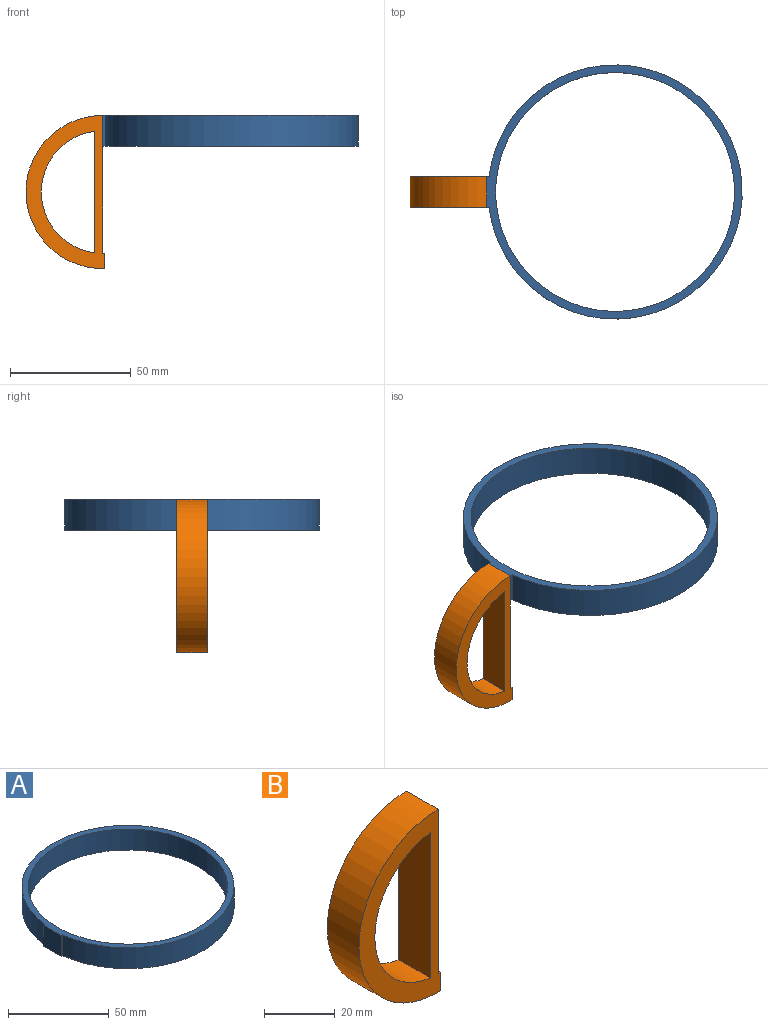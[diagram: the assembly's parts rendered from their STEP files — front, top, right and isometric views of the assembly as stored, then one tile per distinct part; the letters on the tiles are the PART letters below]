
ASSEMBLY  parts=2 mates=1
PART A: 7 faces, bbox 106x105.4x12.7 mm
  f0: plane 12.7x1.02mm, normal (0,-1,0), area 12.9mm2, adj f1,f3,f5,f6
  f1: cylinder r=52.7mm len=105.41mm, axis (0,0,-1), area 4044mm2, adj f0,f2,f5,f6
  f2: plane 12.7x1.02mm, normal (0,1,0), area 12.9mm2, adj f1,f3,f5,f6
  f3: plane 12.7x12.7mm, normal (-1,0,0), area 161.3mm2, adj f0,f2,f5,f6
  f4: cylinder r=49.53mm len=99.06mm, axis (0,0,-1), area 3952.3mm2, adj f5,f6
  f5: plane 106.05x105.41mm, normal (0,0,1), area 1029.4mm2, adj f0,f1,f2,f3,f4
  f6: plane 106.05x105.41mm, normal (0,0,-1), area 1029.4mm2, adj f0,f1,f2,f3,f4
PART B: 9 faces, bbox 32.8x12.7x63.5 mm
  f0: plane 57.15x12.7mm, normal (1,0,0), area 725.8mm2, adj f1,f6,f7,f8
  f1: cylinder r=31.75mm len=63.5mm, axis (0,1,0), area 1279.7mm2, adj f0,f2,f7,f8
  f2: plane 12.7x6.34mm, normal (1,0,0), area 80.5mm2, adj f1,f3,f7,f8
  f3: plane 12.7x0.73mm, normal (0,0,1), area 9.2mm2, adj f2,f6,f7,f8
  f4: cylinder r=25.4mm len=50.4mm, axis (0,1,0), area 932.6mm2, adj f5,f7,f8
  f5: plane 50.4x12.7mm, normal (-1,0,0), area 640.1mm2, adj f4,f7,f8
  f6: cylinder r=25.4mm len=12.7mm, axis (0,1,0), area 3.7mm2, adj f0,f3,f7,f8
  f7: plane 63.5x32.77mm, normal (0,-1,0), area 737.4mm2, adj f0,f1,f2,f3,f4,f5,f6
  f8: plane 63.5x32.77mm, normal (0,1,0), area 737.4mm2, adj f0,f1,f2,f3,f4,f5,f6
PLACE A t=(7.02,-28.3,30.03)mm
PLACE B t=(-46.32,-21.95,10.98)mm
MATE fastened A.f3 <-> B.f0  axis (-1,0,0) through (-46.32,-21.95,42.73)mm
